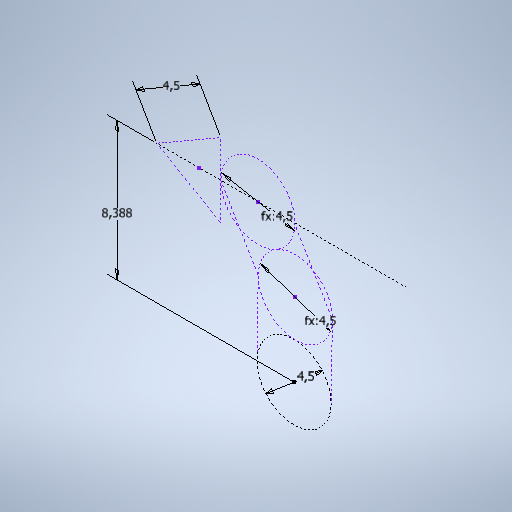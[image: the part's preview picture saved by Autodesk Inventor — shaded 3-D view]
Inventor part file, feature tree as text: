
AUTODESK INVENTOR PART (.ipt)
format: ipt  version: 2025.2 (Build 292293000, 293)  size: 264,192 bytes
history: native  units: mm
features: sketch x1
ambient origin geometry x8: Origin, YZ Plane, XZ Plane, XY Plane, X Axis, Y Axis, Z Axis, Center Point
feature tree (1):
  sketch  "Esboço1"  dims[d0=4.5mm d1=4.5mm d2=4.5mm d3=4.5mm d4=8.387539mm]
